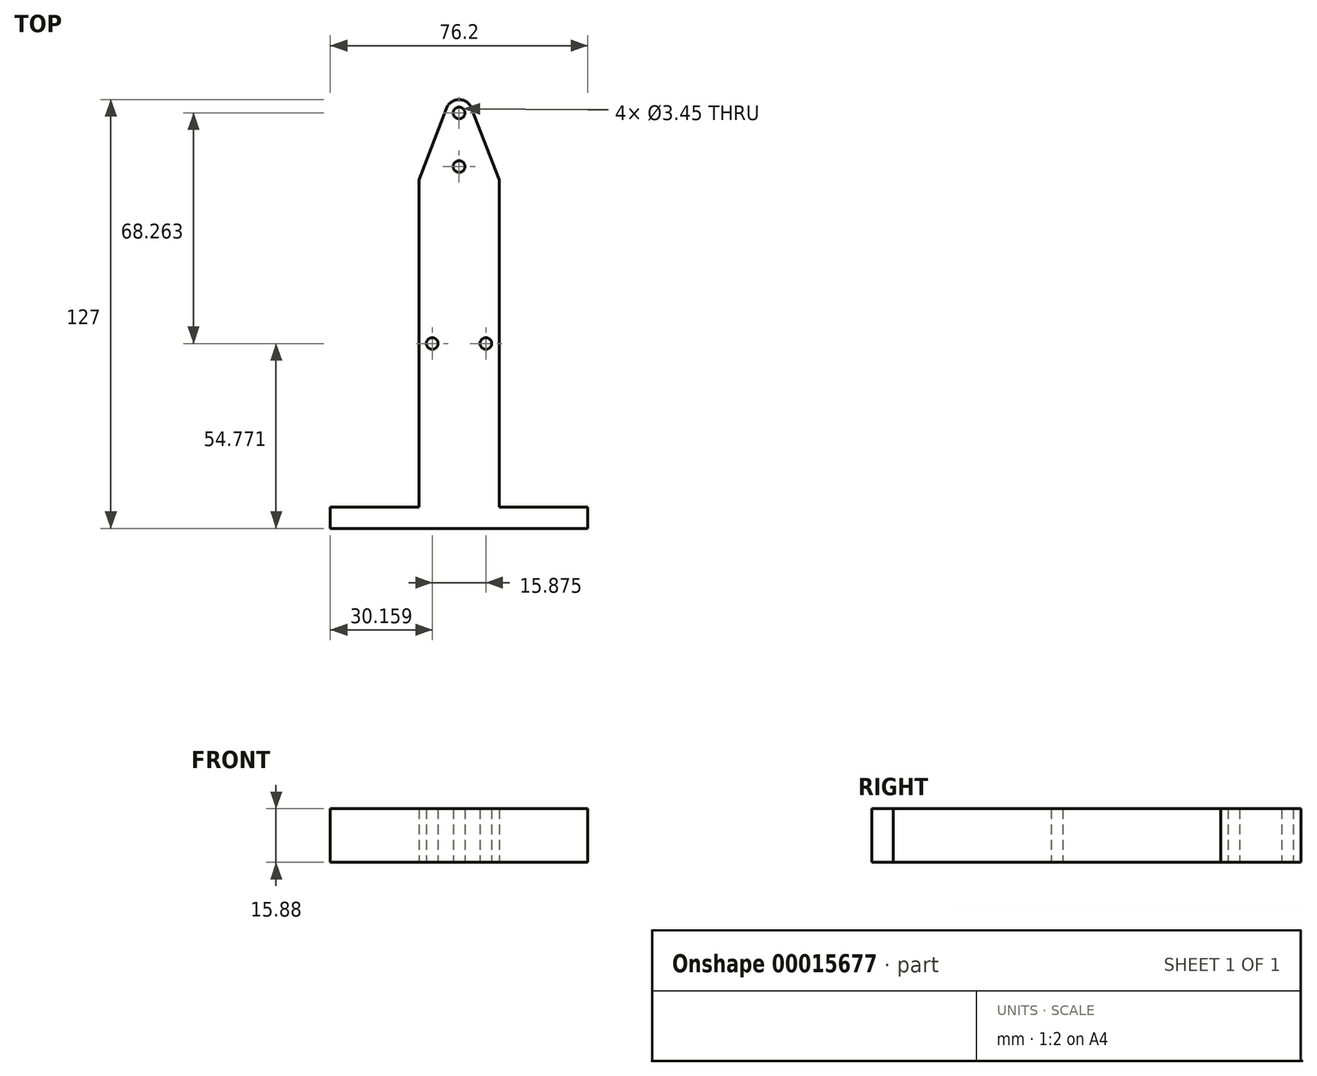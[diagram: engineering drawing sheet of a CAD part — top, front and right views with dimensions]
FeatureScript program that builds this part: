
annotation { "Feature Type Name" : "Feature", "Feature Type Description" : "" }
export const myFeature = defineFeature(function(context is Context, id is Id, definition is map)
    precondition{}
    {
        {
            var Q0;
            Q0=qCreatedBy(makeId("Top.planeOp"),FACE);
            var sketch = newSketch(context, id + "F0", { "sketchPlane" : qUnion([Q0])});
            skLineSegment(sketch, "E0.bottom", {"start": v(0, 0) * mm, "end": v(23.81, 0) * mm, "construction": true});
            skLineSegment(sketch, "E0.top", {"start": v(0, -96.84) * mm, "end": v(23.81, -96.84) * mm, "construction": true});
            skLineSegment(sketch, "E0.left", {"start": v(0, 0) * mm, "end": v(0, -96.84) * mm});
            skLineSegment(sketch, "E0.right", {"start": v(23.81, 0) * mm, "end": v(23.81, -96.84) * mm});
            skLineSegment(sketch, "E1", {"start": v(0, -48.42) * mm, "end": v(3.97, -48.42) * mm});
            skLineSegment(sketch, "E2", {"start": v(3.97, -48.42) * mm, "end": v(11.9, -48.42) * mm});
            skLineSegment(sketch, "E3", {"start": v(11.9, -48.42) * mm, "end": v(19.84, -48.42) * mm, "construction": true});
            skLineSegment(sketch, "E4", {"start": v(19.84, -48.42) * mm, "end": v(23.81, -48.42) * mm, "construction": true});
            skCircle(sketch, "E5", {"center": v(3.97, -48.42) * mm, "radius": 1.73 * mm});
            skCircle(sketch, "E6", {"center": v(19.84, -48.42) * mm, "radius": 1.73 * mm});
            skLineSegment(sketch, "E7", {"start": v(11.9, 0) * mm, "end": v(11.9, 3.97) * mm, "construction": true});
            skLineSegment(sketch, "E8", {"start": v(11.9, 3.97) * mm, "end": v(11.9, 11.9) * mm, "construction": true});
            skLineSegment(sketch, "E9", {"start": v(11.9, 11.9) * mm, "end": v(11.9, 19.84) * mm, "construction": true});
            skLineSegment(sketch, "E10", {"start": v(11.9, 19.84) * mm, "end": v(11.9, 23.81) * mm, "construction": true});
            skArc(sketch, "E11", {"start": v(15.6, 21.27) * mm, "mid": v(11.9, 23.81) * mm, "end": v(8.2, 21.27) * mm});
            skLineSegment(sketch, "E12", {"start": v(0, 0) * mm, "end": v(8.2, 21.27) * mm});
            skLineSegment(sketch, "E13", {"start": v(15.6, 21.27) * mm, "end": v(23.81, 0) * mm});
            skCircle(sketch, "E14", {"center": v(11.9, 19.84) * mm, "radius": 1.73 * mm});
            skCircle(sketch, "E15", {"center": v(11.9, 3.97) * mm, "radius": 1.73 * mm});
            skLineSegment(sketch, "E16.top", {"start": v(-26.2, -103.19) * mm, "end": v(50, -103.19) * mm});
            skLineSegment(sketch, "E16.left", {"start": v(-26.2, -96.84) * mm, "end": v(-26.2, -103.19) * mm});
            skLineSegment(sketch, "E16.right", {"start": v(50, -96.84) * mm, "end": v(50, -103.19) * mm});
            skLineSegment(sketch, "E17", {"start": v(23.81, -96.84) * mm, "end": v(50, -96.84) * mm});
            skLineSegment(sketch, "E18", {"start": v(0, -96.84) * mm, "end": v(-26.2, -96.84) * mm});
            skSolve(sketch);
        }
        {
            var Q0;
            Q0=qSketchRegion(id+"F0",true);
            extrude(context, id + "F1", {"entities" : qUnion([Q0]), "depth" : 15.88 * mm});
        }
    });
